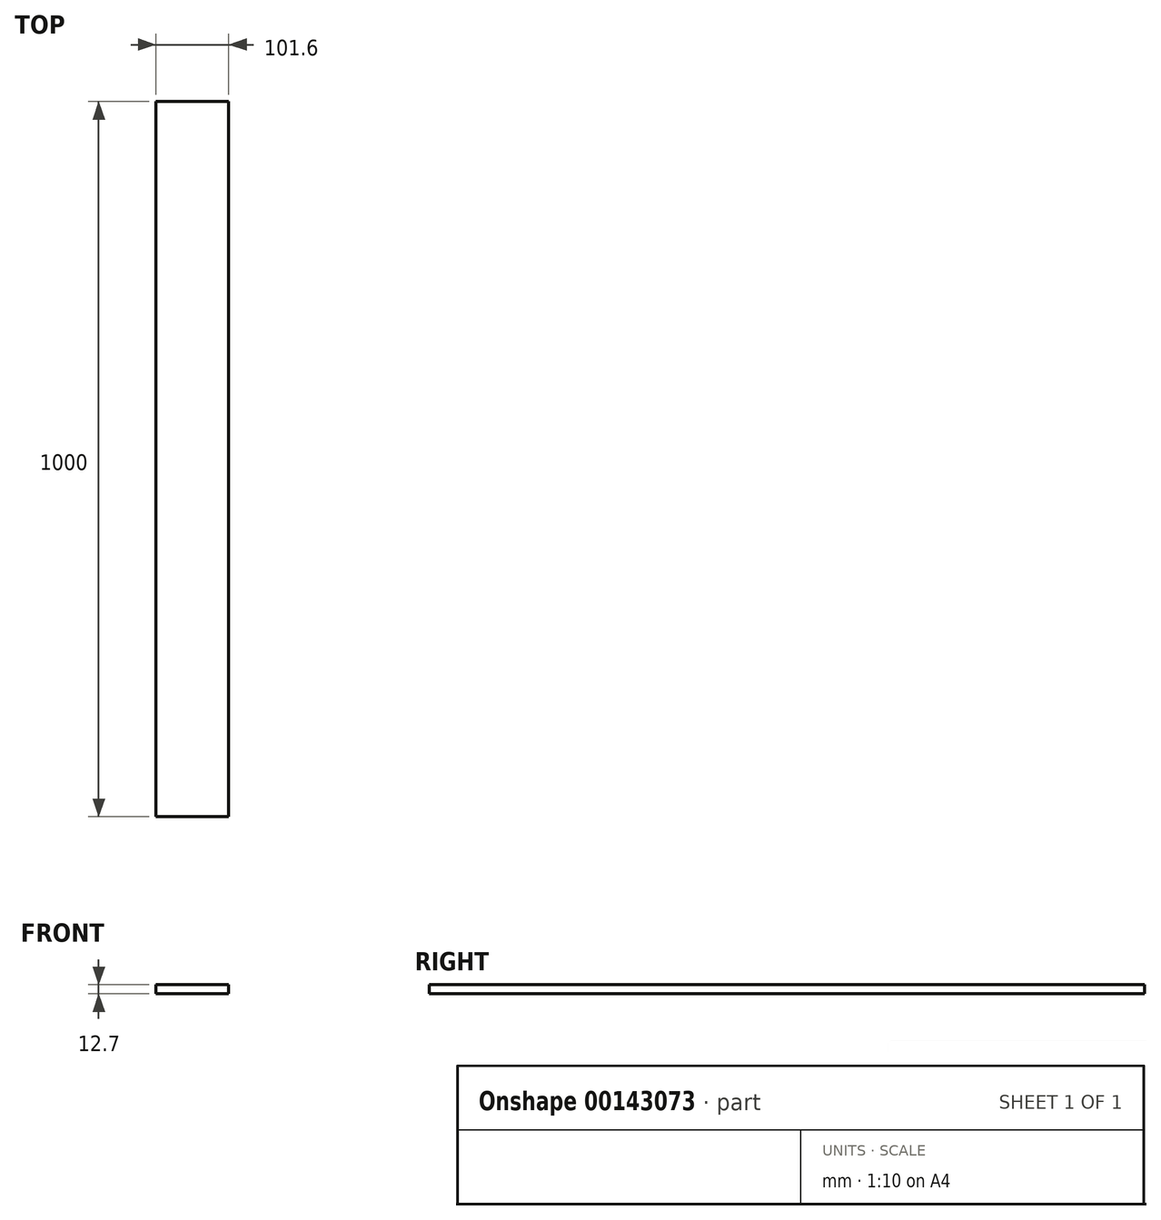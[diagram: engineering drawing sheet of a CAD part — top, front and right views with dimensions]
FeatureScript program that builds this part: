
annotation { "Feature Type Name" : "Feature", "Feature Type Description" : "" }
export const myFeature = defineFeature(function(context is Context, id is Id, definition is map)
    precondition{}
    {
        {
            var Q0;
            Q0=qCreatedBy(makeId("Front.planeOp"),FACE);
            var sketch = newSketch(context, id + "F0", { "sketchPlane" : qUnion([Q0])});
            skLineSegment(sketch, "E0.bottom", {"start": v(-50.8, 6.35) * mm, "end": v(50.8, 6.35) * mm});
            skLineSegment(sketch, "E0.top", {"start": v(-50.8, -6.35) * mm, "end": v(50.8, -6.35) * mm});
            skLineSegment(sketch, "E0.left", {"start": v(-50.8, 6.35) * mm, "end": v(-50.8, -6.35) * mm});
            skLineSegment(sketch, "E0.right", {"start": v(50.8, 6.35) * mm, "end": v(50.8, -6.35) * mm});
            skPoint(sketch, "E0.middle", {"position": v(0, 0) * mm});
            skSolve(sketch);
        }
        {
            var Q0;
            Q0 = qSketchRegion(id + "F0", true);
            extrude(context, id + "F1", {"entities" : qUnion([Q0]), "depth" : 1000 * mm});
        }
    });
